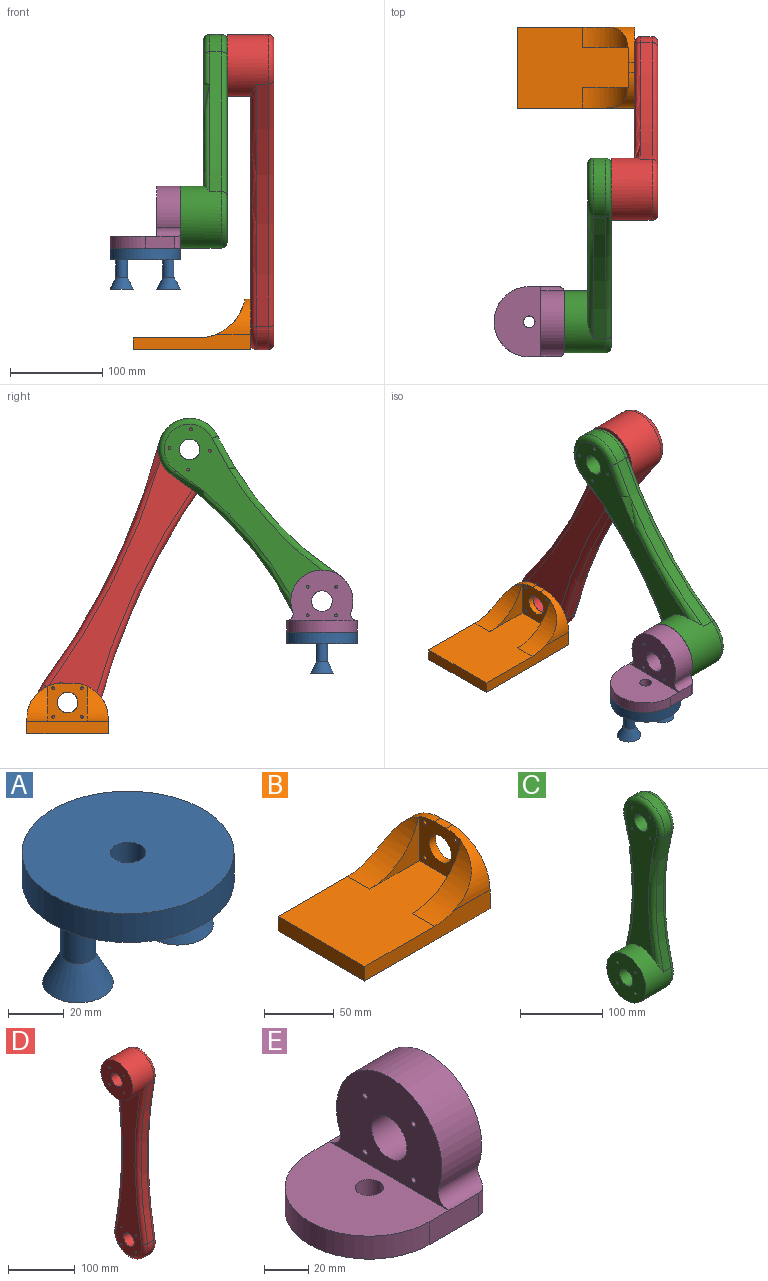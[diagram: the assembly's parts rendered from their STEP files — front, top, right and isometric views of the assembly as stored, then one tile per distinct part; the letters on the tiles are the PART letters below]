
ASSEMBLY  parts=5 mates=5
PART A: 18 faces, bbox 76.2x76.2x44.5 mm
  f0: cylinder r=6.35mm len=12.7mm, axis (0,0,1), area 506.7mm2, adj f2,f3
  f1: cylinder r=38.1mm len=76.2mm, axis (0,0,1), area 3040.2mm2, adj f2,f3
  f2: plane 76.2x76.2mm, normal (0,0,-1), area 4180.3mm2, adj f0,f1,f4,f5
  f3: plane 76.2x76.2mm, normal (0,0,1), area 4433.7mm2, adj f0,f1
  f4: cylinder r=6.35mm len=19.05mm, axis (0,0,1), area 760.1mm2, adj f2,f9
  f5: cylinder r=6.35mm len=19.05mm, axis (0,0,1), area 760.1mm2, adj f2,f7
  f6: plane 25.4x25.4mm, normal (0,0,-1), area 201.3mm2, adj f7,f16
  f7: cone r=6.35mm half-angle=26.6deg, axis (0,0,-1), area 849.8mm2, adj f5,f6
  f8: plane 25.4x25.4mm, normal (0,0,-1), area 201.3mm2, adj f9,f17
  f9: cone r=6.35mm half-angle=26.6deg, axis (0,0,-1), area 849.8mm2, adj f4,f8
  f10: cylinder r=8.89mm len=17.78mm, axis (0,0,1), area 425.6mm2, adj f12,f13
  f11: cylinder r=35.56mm len=71.12mm, axis (0,0,1), area 1702.5mm2, adj f12,f13
  f12: plane 71.12x71.12mm, normal (0,0,1), area 3633.1mm2, adj f10,f11,f14,f15
  f13: plane 71.12x71.12mm, normal (0,0,-1), area 3724.3mm2, adj f10,f11
  f14: cylinder r=3.81mm len=22.19mm, axis (0,0,1), area 531.2mm2, adj f12,f17
  f15: cylinder r=3.81mm len=22.19mm, axis (0,0,1), area 531.2mm2, adj f12,f16
  f16: cone r=4.08mm half-angle=26.6deg, axis (0,0,-1), area 581mm2, adj f6,f15
  f17: cone r=4.08mm half-angle=26.6deg, axis (0,0,-1), area 581mm2, adj f8,f14
PART B: 19 faces, bbox 127x88x54.7 mm
  f0: cylinder r=11.25mm len=22.5mm, axis (-1,0,0), area 448.9mm2, adj f7,f16
  f1: cylinder r=1.5mm len=6.35mm, axis (-1,0,0), area 59.8mm2, adj f7,f16
  f2: cylinder r=1.5mm len=6.35mm, axis (-1,0,0), area 59.8mm2, adj f7,f16
  f3: cylinder r=1.5mm len=6.35mm, axis (-1,0,0), area 59.8mm2, adj f7,f16
  f4: cylinder r=1.5mm len=6.35mm, axis (-1,0,0), area 59.8mm2, adj f7,f16
  f5: cylinder r=38.1mm len=38.1mm, axis (-1,0,0), area 784.5mm2, adj f6,f7,f10,f13,f16,f18
  f6: cylinder r=50.8mm len=49.33mm, axis (0,-1,0), area 1275.8mm2, adj f5,f10,f11,f18
  f7: plane 88.01x54.7mm, normal (1,0,0), area 3765.3mm2, adj f0,f1,f2,f3,f4,f5,f8,f10
  f8: plane 127x16.6mm, normal (0,1,0), area 1781.6mm2, adj f7,f9,f11,f12,f14,f15
  f9: plane 88.01x12.7mm, normal (-1,0,0), area 1117.7mm2, adj f8,f10,f11,f12
  f10: plane 127x16.6mm, normal (0,-1,0), area 1781.6mm2, adj f5,f6,f7,f9,f11,f12
  f11: plane 120.65x88.01mm, normal (0,0,1), area 8366.5mm2, adj f6,f8,f9,f10,f15,f16,f17,f18
  f12: plane 127x88.01mm, normal (0,0,-1), area 11177.4mm2, adj f7,f8,f9,f10
  f13: plane 11.81x6.35mm, normal (0,0,1), area 75mm2, adj f5,f7,f14,f16
  f14: cylinder r=38.1mm len=38.1mm, axis (1,0,0), area 784.5mm2, adj f7,f8,f13,f15,f16,f17
  f15: cylinder r=50.8mm len=49.33mm, axis (0,-1,0), area 1275.9mm2, adj f8,f11,f14,f17
  f16: plane 43x42mm, normal (-1,0,0), area 1346.1mm2, adj f0,f1,f2,f3,f4,f5,f11,f13
  f17: plane 50.03x38.66mm, normal (0,-1,0), area 518.2mm2, adj f11,f14,f15,f16
  f18: plane 50.03x38.66mm, normal (0,1,0), area 518.2mm2, adj f5,f6,f11,f16
PART C: 24 faces, bbox 50.8x73x291.3 mm
  f0: plane 220.02x54.7mm, normal (-1,0,0), area 7038.7mm2, adj f3,f9,f10,f11,f12,f13,f21,f22
  f1: cylinder r=33.7mm len=67.4mm, axis (1,0,0), area 1572.9mm2, adj f2,f8,f19,f22
  f2: cylinder r=380.42mm len=200.58mm, axis (1,0,0), area 2577.9mm2, adj f1,f3,f17,f21
  f3: cylinder r=33.7mm len=67.4mm, axis (1,0,0), area 7836.7mm2, adj f0,f2,f8,f16,f18,f21,f23
  f4: cylinder r=1.5mm len=50.8mm, axis (1,0,0), area 478.8mm2, adj f15,f16
  f5: cylinder r=1.5mm len=50.8mm, axis (1,0,0), area 478.8mm2, adj f15,f16
  f6: cylinder r=1.5mm len=50.8mm, axis (1,0,0), area 478.8mm2, adj f15,f16
  f7: cylinder r=1.5mm len=50.8mm, axis (1,0,0), area 478.8mm2, adj f15,f16
  f8: cylinder r=380.42mm len=200.58mm, axis (1,0,0), area 2577.9mm2, adj f1,f3,f20,f23
  f9: cylinder r=1.5mm len=25.4mm, axis (1,0,0), area 239.4mm2, adj f0,f15
  f10: cylinder r=1.5mm len=25.4mm, axis (1,0,0), area 239.4mm2, adj f0,f15
  f11: cylinder r=11.25mm len=25.4mm, axis (1,0,0), area 1795.4mm2, adj f0,f15
  f12: cylinder r=1.5mm len=25.4mm, axis (1,0,0), area 239.4mm2, adj f0,f15
  f13: cylinder r=1.5mm len=25.4mm, axis (1,0,0), area 239.4mm2, adj f0,f15
  f14: cylinder r=11.25mm len=50.8mm, axis (1,0,0), area 3590.8mm2, adj f15,f16
  f15: plane 273.05x54.7mm, normal (1,0,0), area 9304.4mm2, adj f4,f5,f6,f7,f9,f10,f11,f12
  f16: plane 67.4x67.4mm, normal (-1,0,0), area 3142mm2, adj f3,f4,f5,f6,f7,f14
  f17: torus R=386.77mm, axis (-1,0,0), area 2036.9mm2, adj f2,f15,f18,f19
  f18: torus R=27.35mm, axis (-1,0,0), area 1150.8mm2, adj f3,f15,f17,f20
  f19: torus R=27.35mm, axis (-1,0,0), area 1150.8mm2, adj f1,f15,f17,f20
  f20: torus R=386.77mm, axis (-1,0,0), area 2036.9mm2, adj f8,f15,f18,f19
  f21: torus R=386.77mm, axis (-1,0,0), area 1934.8mm2, adj f0,f2,f3,f22
  f22: torus R=27.35mm, axis (-1,0,0), area 1150.8mm2, adj f0,f1,f21,f23
  f23: torus R=386.77mm, axis (-1,0,0), area 1934.8mm2, adj f0,f3,f8,f22
PART D: 24 faces, bbox 50.8x73x377.8 mm
  f0: cylinder r=766.31mm len=291.96mm, axis (-1,0,0), area 3730.7mm2, adj f1,f12,f19,f20
  f1: cylinder r=33.7mm len=67.4mm, axis (-1,0,0), area 1508.6mm2, adj f0,f2,f18,f21
  f2: cylinder r=766.31mm len=291.96mm, axis (-1,0,0), area 3730.7mm2, adj f1,f12,f17,f23
  f3: cylinder r=1.5mm len=25.4mm, axis (-1,0,0), area 239.4mm2, adj f14,f15
  f4: cylinder r=11.25mm len=25.4mm, axis (-1,0,0), area 1795.4mm2, adj f14,f15
  f5: cylinder r=1.5mm len=25.4mm, axis (-1,0,0), area 239.4mm2, adj f14,f15
  f6: cylinder r=1.5mm len=25.4mm, axis (-1,0,0), area 239.4mm2, adj f14,f15
  f7: cylinder r=1.5mm len=50.8mm, axis (-1,0,0), area 478.8mm2, adj f14,f16
  f8: cylinder r=1.5mm len=50.8mm, axis (-1,0,0), area 478.8mm2, adj f14,f16
  f9: cylinder r=11.25mm len=50.8mm, axis (-1,0,0), area 3590.8mm2, adj f14,f16
  f10: cylinder r=1.5mm len=50.8mm, axis (-1,0,0), area 478.8mm2, adj f14,f16
  f11: cylinder r=1.5mm len=50.8mm, axis (-1,0,0), area 478.8mm2, adj f14,f16
  f12: cylinder r=33.7mm len=67.4mm, axis (-1,0,0), area 7742.3mm2, adj f0,f2,f15,f16,f17,f19,f22
  f13: cylinder r=1.5mm len=25.4mm, axis (-1,0,0), area 239.4mm2, adj f14,f15
  f14: plane 359.5x54.7mm, normal (1,0,0), area 12308.6mm2, adj f3,f4,f5,f6,f7,f8,f9,f10
  f15: plane 307.9x54.7mm, normal (-1,0,0), area 10016.7mm2, adj f3,f4,f5,f6,f12,f13,f17,f18
  f16: plane 67.4x67.4mm, normal (-1,0,0), area 3142mm2, adj f7,f8,f9,f10,f11,f12
  f17: torus R=772.66mm, axis (1,0,0), area 2834.9mm2, adj f2,f12,f15,f18
  f18: torus R=27.35mm, axis (1,0,0), area 1103.7mm2, adj f1,f15,f17,f19
  f19: torus R=772.66mm, axis (1,0,0), area 2834.9mm2, adj f0,f12,f15,f18
  f20: torus R=772.66mm, axis (1,0,0), area 2938.9mm2, adj f0,f14,f21,f22
  f21: torus R=27.35mm, axis (1,0,0), area 1103.7mm2, adj f1,f14,f20,f23
  f22: torus R=27.35mm, axis (1,0,0), area 1103.7mm2, adj f12,f14,f20,f23
  f23: torus R=772.66mm, axis (1,0,0), area 2938.9mm2, adj f2,f14,f21,f22
PART E: 18 faces, bbox 76.2x76.2x67.4 mm
  f0: plane 76.2x54.7mm, normal (-1,0,0), area 2731.7mm2, adj f1,f2,f3,f6,f7,f8,f9,f11
  f1: cylinder r=6.92mm len=25.4mm, axis (1,0,0), area 329.2mm2, adj f0,f2,f10,f12,f15
  f2: cylinder r=33.7mm len=67.4mm, axis (1,0,0), area 3295.2mm2, adj f0,f1,f3,f12
  f3: cylinder r=6.92mm len=25.4mm, axis (1,0,0), area 329.2mm2, adj f0,f2,f4,f12,f16
  f4: plane 31.75x12.7mm, normal (0,1,0), area 403.2mm2, adj f3,f5,f13,f14,f16
  f5: plane 76.2x76.2mm, normal (0,0,-1), area 5039.4mm2, adj f4,f10,f12,f14,f15,f16,f17
  f6: cylinder r=1.5mm len=25.4mm, axis (1,0,0), area 239.4mm2, adj f0,f12
  f7: cylinder r=11.25mm len=25.4mm, axis (1,0,0), area 1795.4mm2, adj f0,f12
  f8: cylinder r=1.5mm len=25.4mm, axis (1,0,0), area 239.4mm2, adj f0,f12
  f9: cylinder r=1.5mm len=25.4mm, axis (1,0,0), area 239.4mm2, adj f0,f12
  f10: plane 31.75x12.7mm, normal (0,-1,0), area 403.2mm2, adj f1,f5,f13,f14,f15
  f11: cylinder r=1.5mm len=25.4mm, axis (1,0,0), area 239.4mm2, adj f0,f12
  f12: plane 67.4x67.4mm, normal (1,0,0), area 3523.3mm2, adj f1,f2,f3,f5,f6,f7,f8,f9
  f13: plane 76.2x50.8mm, normal (0,0,1), area 3121.2mm2, adj f0,f4,f10,f14,f17
  f14: cylinder r=38.1mm len=76.2mm, axis (0,0,-1), area 1520.1mm2, adj f4,f5,f10,f13
  f15: cylinder r=6.35mm len=16.87mm, axis (0,0,1), area 134.5mm2, adj f1,f5,f10,f12
  f16: cylinder r=6.35mm len=16.87mm, axis (0,0,-1), area 134.5mm2, adj f3,f4,f5,f12
  f17: cylinder r=6.35mm len=12.7mm, axis (0,0,1), area 506.7mm2, adj f5,f13
PLACE A t=(-123.72,-228.28,-16.82)mm
PLACE B t=(-98.32,47.68,-40.43)mm fixed
PLACE C rot(axis=(-1,0,0),41.1deg) t=(-123.72,-307.29,12.81)mm
PLACE D rot(axis=(1,0,0),25.7deg) t=(-98.32,62.32,-37.09)mm
PLACE E t=(-123.72,-228.28,-16.82)mm
MATE revolute D.f12 <-> C.f11  axis (-1,0,0) through (-60.22,-84.69,267.83)mm
MATE parallel B.f11 <-> E.f14  axis (0,0,1) through (-111,47.68,-27.73)mm
MATE revolute C.f14 <-> E.f7  axis (-1,0,0) through (-111.02,-228.28,103.33)mm
MATE revolute E.f14 <-> A.f1  axis (0,0,-1) through (-149.12,-228.28,69.63)mm
MATE revolute B.f0 <-> D.f4  axis (1,0,0) through (-34.82,47.68,-6.73)mm
